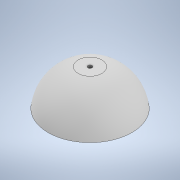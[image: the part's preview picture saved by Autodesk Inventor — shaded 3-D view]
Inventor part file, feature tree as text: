
AUTODESK INVENTOR PART (.ipt)
format: ipt  version: 2022 (Build 260153000, 153)  size: 136,704 bytes
history: native  units: in
note: dims shown in document units (in); Inventor stores cm internally (conversion verified against a paired STEP export)
features: sketch x5, extrude x4, revolve x1
ambient origin geometry x8: Origin, YZ Plane, XZ Plane, XY Plane, X Axis, Y Axis, Z Axis, Center Point
bodies: Solid1 (feature_tree)
feature tree (10):
  revolve  "Revolution1"  [1 undecoded]
  extrude  "Extrusion1"  Depth=1.0in
  extrude  "Extrusion2"  Depth=0.125in
  extrude  "Extrusion3"  Depth=0.125in TaperAngle=0.0deg
  extrude  "Extrusion4"  Depth=0.0344in
  sketch  "Sketch1"  dims[d4=180.0deg d5=1.2in d6=0.0in]
  sketch  "Sketch2"  dims[d7=1.1in d8=1.0in]
  sketch  "Sketch3"  dims[d9=0.125in d10=0.0in d11=0.125in]
  sketch  "Sketch4"  dims[d12=0.25in d13=0.0in d14=0.125in d15=0.0in]
  sketch  "Sketch5"  dims[d16=0.5in d17=0.0344in d18=0.5in d19=0.0344in]
note: 1 required parameter value undecoded (feature->parameter linkage not recoverable at this tier; creation-order binding heuristic only, values carry confidence <= 0.55)
